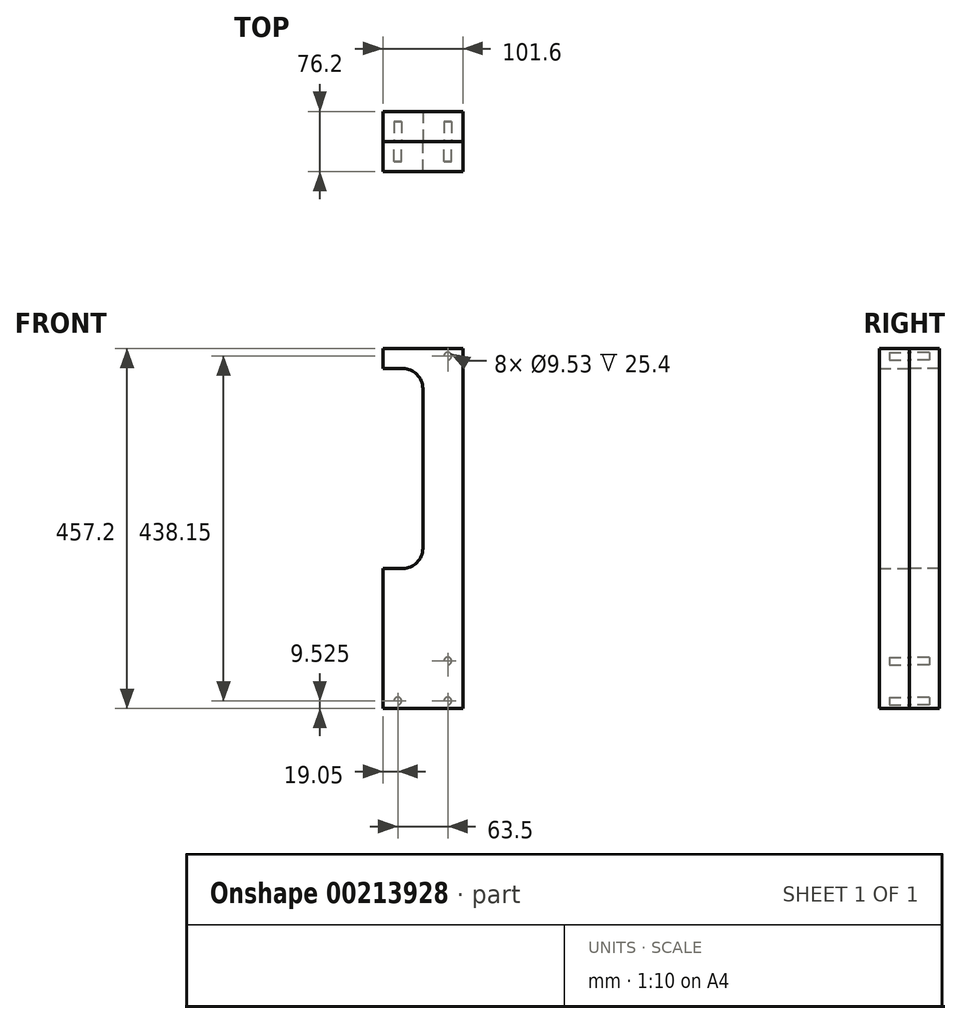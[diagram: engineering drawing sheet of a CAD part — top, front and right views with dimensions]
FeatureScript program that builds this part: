
annotation { "Feature Type Name" : "Feature", "Feature Type Description" : "" }
export const myFeature = defineFeature(function(context is Context, id is Id, definition is map)
    precondition{}
    {
        {
            var Q0;
            Q0=qCreatedBy(makeId("Front.planeOp"),FACE);
            var sketch = newSketch(context, id + "F0", { "sketchPlane" : qUnion([Q0])});
            skLineSegment(sketch, "E0.bottom", {"start": v(50.8, 228.6) * mm, "end": v(-50.8, 228.6) * mm});
            skLineSegment(sketch, "E0.top", {"start": v(50.8, -228.6) * mm, "end": v(-50.8, -228.6) * mm});
            skLineSegment(sketch, "E0.left", {"start": v(50.8, 228.6) * mm, "end": v(50.8, -228.6) * mm});
            skLineSegment(sketch, "E0.right", {"start": v(-50.8, 228.6) * mm, "end": v(-50.8, 203.2) * mm});
            skPoint(sketch, "E0.middle", {"position": v(0, 0) * mm});
            skLineSegment(sketch, "E1", {"start": v(-50.8, 203.2) * mm, "end": v(-25.4, 203.2) * mm});
            skArc(sketch, "E2", {"start": v(-25.4, 203.2) * mm, "mid": v(-7.44, 195.76) * mm, "end": v(0, 177.8) * mm});
            skLineSegment(sketch, "E3", {"start": v(0, 177.8) * mm, "end": v(0, -25.4) * mm});
            skArc(sketch, "E4", {"start": v(0, -25.4) * mm, "mid": v(-7.44, -43.36) * mm, "end": v(-25.4, -50.8) * mm});
            skLineSegment(sketch, "E5", {"start": v(-25.4, -50.8) * mm, "end": v(-50.8, -50.8) * mm});
            skLineSegment(sketch, "E6.trimOffspring", {"start": v(-50.8, -50.8) * mm, "end": v(-50.8, -228.6) * mm});
            skSolve(sketch);
        }
        {
            var Q0;
            Q0 = qSketchRegion(id + "F0", true);
            extrude(context, id + "F1", {"entities" : qUnion([Q0]), "depth" : 38.1 * mm});
        }
        {
            var Q0;
            Q0=makeQuery(id+"F1.opExtrude","CAP_FACE",FACE,{"disambiguationData":[OSD([sQuery(id+"F0.wireOp",EDGE,"E0.bottom"),sQuery(id+"F0.wireOp",EDGE,"E0.top"),sQuery(id+"F0.wireOp",EDGE,"E0.left"),sQuery(id+"F0.wireOp",EDGE,"E0.right"),sQuery(id+"F0.wireOp",EDGE,"E1"),sQuery(id+"F0.wireOp",EDGE,"E2"),sQuery(id+"F0.wireOp",EDGE,"E3"),sQuery(id+"F0.wireOp",EDGE,"E4"),sQuery(id+"F0.wireOp",EDGE,"E5"),sQuery(id+"F0.wireOp",EDGE,"E6.trimOffspring")])],"isStart":true});
            var sketch = newSketch(context, id + "F2", { "sketchPlane" : qUnion([Q0])});
            skCircle(sketch, "E7", {"center": v(-31.75, -219.08) * mm, "radius": 4.76 * mm});
            skCircle(sketch, "E8.1.0.0", {"center": v(31.75, -219.08) * mm, "radius": 4.76 * mm});
            skLineSegment(sketch, "E8.direction1", {"start": v(-31.75, -219.08) * mm, "end": v(31.75, -219.08) * mm, "construction": true});
            skCircle(sketch, "E9.0.1.0", {"center": v(-31.75, -168.28) * mm, "radius": 4.76 * mm});
            skLineSegment(sketch, "E9.direction1", {"start": v(-31.75, -219.08) * mm, "end": v(-12.7, -219.08) * mm, "construction": true});
            skLineSegment(sketch, "E9.direction2", {"start": v(-31.75, -219.08) * mm, "end": v(-31.75, -168.28) * mm, "construction": true});
            skSolve(sketch);
        }
        {
            var Q0;
            Q0 = qSketchRegion(id + "F2", true);
            extrude(context, id + "F3", {"entities" : qUnion([Q0]), "operationType" : NewBodyOperationType.REMOVE, "oppositeDirection" : true, "depth" : 25.4 * mm});
        }
        {
            var Q0;
            Q0=makeQuery(id+"F1.opExtrude","CAP_FACE",FACE,{"disambiguationData":[OSD([sQuery(id+"F0.wireOp",EDGE,"E0.bottom"),sQuery(id+"F0.wireOp",EDGE,"E0.top"),sQuery(id+"F0.wireOp",EDGE,"E0.left"),sQuery(id+"F0.wireOp",EDGE,"E0.right"),sQuery(id+"F0.wireOp",EDGE,"E1"),sQuery(id+"F0.wireOp",EDGE,"E2"),sQuery(id+"F0.wireOp",EDGE,"E3"),sQuery(id+"F0.wireOp",EDGE,"E4"),sQuery(id+"F0.wireOp",EDGE,"E5"),sQuery(id+"F0.wireOp",EDGE,"E6.trimOffspring")])],"isStart":true});
            var sketch = newSketch(context, id + "F4", { "sketchPlane" : qUnion([Q0])});
            skCircle(sketch, "E10", {"center": v(-31.75, 219.08) * mm, "radius": 4.76 * mm});
            skSolve(sketch);
        }
        {
            var Q0;
            Q0 = qSketchRegion(id + "F4", true);
            extrude(context, id + "F5", {"entities" : qUnion([Q0]), "operationType" : NewBodyOperationType.REMOVE, "oppositeDirection" : true, "depth" : 25.4 * mm});
        }
        {
            var Q0;
            Q0=makeQuery(id+"F1.opExtrude","SWEPT_BODY",BODY,{"disambiguationData":[OSD([sQuery(id+"F0.wireOp",EDGE,"E0.bottom"),sQuery(id+"F0.wireOp",EDGE,"E0.top"),sQuery(id+"F0.wireOp",EDGE,"E0.left"),sQuery(id+"F0.wireOp",EDGE,"E0.right"),sQuery(id+"F0.wireOp",EDGE,"E1"),sQuery(id+"F0.wireOp",EDGE,"E2"),sQuery(id+"F0.wireOp",EDGE,"E3"),sQuery(id+"F0.wireOp",EDGE,"E4"),sQuery(id+"F0.wireOp",EDGE,"E5"),sQuery(id+"F0.wireOp",EDGE,"E6.trimOffspring")])]});
            var Q1;
            Q1=qCreatedBy(makeId("Front.planeOp"),FACE);
            mirror(context, id + "F6", {"entities" : qUnion([Q0]), "mirrorPlane" : qUnion([Q1])});
        }
    });
